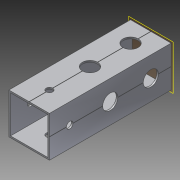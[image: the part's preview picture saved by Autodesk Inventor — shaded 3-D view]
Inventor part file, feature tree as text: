
AUTODESK INVENTOR PART (.ipt)
format: ipt  version: 2014 SP1 (Build 180222100, 222)  size: 1,225,216 bytes
history: native  units: in
note: dims shown in document units (in); Inventor stores cm internally (conversion verified against a paired STEP export)
features: extrude x3, sketch x3, pattern_circular x1, other x1, plane x1, imported_body x1
ambient origin geometry x8: Origin, YZ Plane, XZ Plane, XY Plane, X Axis, Y Axis, Z Axis, Center Point
bodies: Body1 (feature_tree)
feature tree (10):
  pattern_circular  "CirPattern2"
  other  "217-3426-STEP1"
  plane  "Work Plane1"
  extrude  "Extrusion1"  Depth=3937.0079in TaperAngle=0.0deg
  extrude  "Extrusion2"  Depth=0.375in
  extrude  "Extrusion3"  Depth=0.375in
  imported_body  "Base1"
  sketch  "Sketch1"  dims[d0=-3.0in d1=3937.0079in d2=0.0in]
  sketch  "Sketch3"  dims[d3=0.375in d4=0.375in]
  sketch  "Sketch4"  dims[d5=39.3701in d6=0.0in d7=0.375in d8=0.375in d9=39.3701in d10=0.0in]
